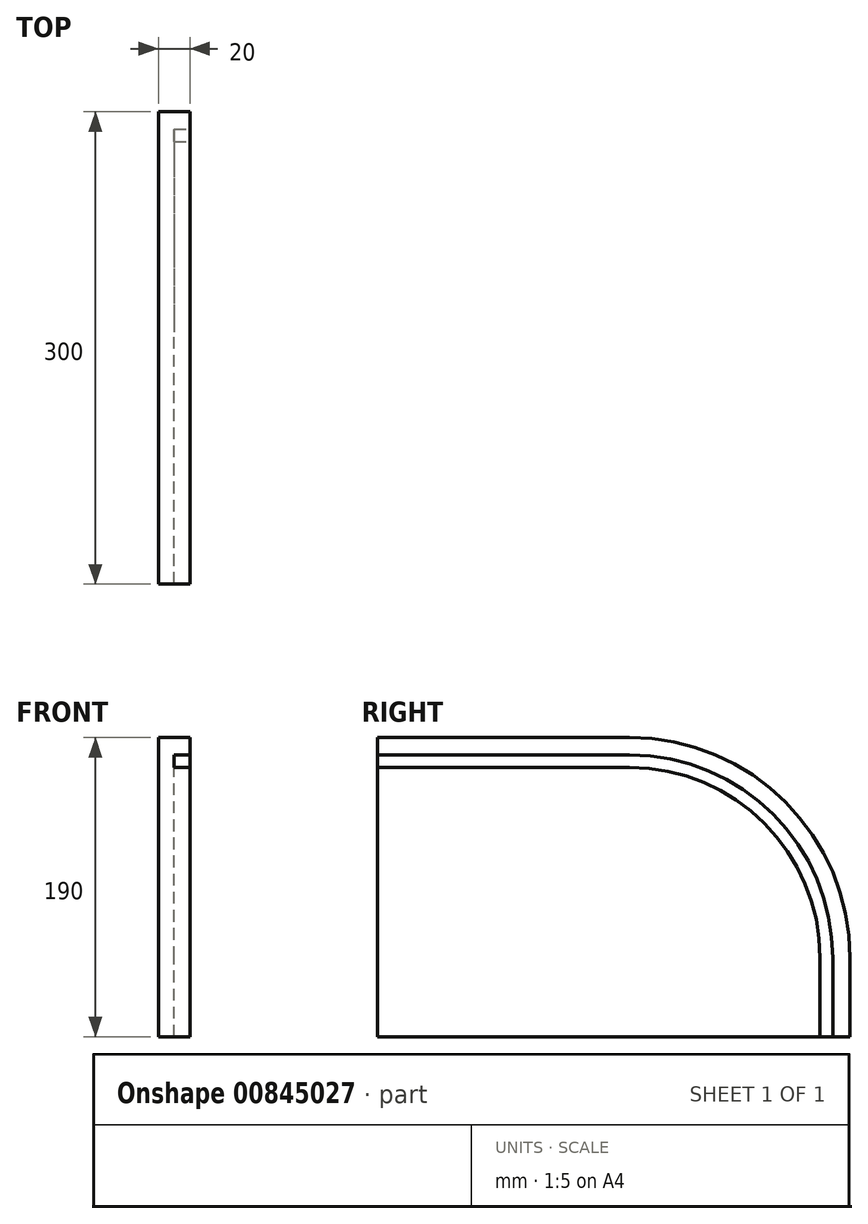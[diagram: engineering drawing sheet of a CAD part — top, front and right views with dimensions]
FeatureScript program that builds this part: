
annotation { "Feature Type Name" : "Feature", "Feature Type Description" : "" }
export const myFeature = defineFeature(function(context is Context, id is Id, definition is map)
    precondition{}
    {
        {
            var Q0;
            Q0=qCreatedBy(makeId("Right.planeOp"),FACE);
            var sketch = newSketch(context, id + "F0", { "sketchPlane" : qUnion([Q0])});
            skLineSegment(sketch, "E0.bottom", {"start": v(-150, 95) * mm, "end": v(150, 95) * mm});
            skLineSegment(sketch, "E0.top", {"start": v(-150, -95) * mm, "end": v(150, -95) * mm});
            skLineSegment(sketch, "E0.left", {"start": v(-150, 95) * mm, "end": v(-150, -95) * mm});
            skLineSegment(sketch, "E0.right", {"start": v(150, 95) * mm, "end": v(150, -95) * mm});
            skPoint(sketch, "E0.middle", {"position": v(0, 0) * mm});
            skLineSegment(sketch, "E1", {"start": v(150, -95) * mm, "end": v(-150, -95) * mm});
            skSolve(sketch);
        }
        {
            var Q0;
            Q0=makeQuery(id+"F0.imprint","IMPRINT",FACE,{"disambiguationData":[TD([[makeQuery(id+"F0.imprint","IMPRINT",EDGE,{"derivedFrom":sQuery(id+"F0.wireOp",EDGE,"E0.bottom")}),-1.0]])]});
            extrude(context, id + "F1", {"entities" : qUnion([Q0]), "depth" : 20 * mm, "offsetDistance" : 25 * mm});
        }
        {
            var Q0;
            Q0=makeQuery(id+"F1.opExtrude","SWEPT_EDGE",EDGE,{"disambiguationData":[OSD([sQuery(id+"F0.wireOp",EDGE,"E0.bottom"),sQuery(id+"F0.wireOp",EDGE,"E0.right")])]});
            fillet(context, id + "F2", {"entities" : qUnion([Q0]), "radius" : 140 * mm, "tangentPropagation" : true, "allowEdgeOverflow" : false});
        }
        {
            var Q0;
            Q0=makeQuery(id+"F1.opExtrude","CAP_FACE",FACE,{"disambiguationData":[OSD([sQuery(id+"F0.wireOp",EDGE,"E0.bottom"),sQuery(id+"F0.wireOp",EDGE,"E0.left"),sQuery(id+"F0.wireOp",EDGE,"E0.right"),sQuery(id+"F0.wireOp",EDGE,"E1")])],"isStart":false});
            var sketch = newSketch(context, id + "F3", { "sketchPlane" : qUnion([Q0])});
            skPoint(sketch, "E2", {"position": v(139, -95) * mm});
            skPoint(sketch, "E3", {"position": v(131, -95) * mm});
            skPoint(sketch, "E4", {"position": v(-150, 84) * mm});
            skPoint(sketch, "E5", {"position": v(-150, 76) * mm});
            skLineSegment(sketch, "E6", {"start": v(139, -95) * mm, "end": v(139, -45) * mm});
            skLineSegment(sketch, "E7", {"start": v(131, -95) * mm, "end": v(131, -45) * mm});
            skLineSegment(sketch, "E8", {"start": v(-150, 84) * mm, "end": v(10, 84) * mm});
            skLineSegment(sketch, "E9", {"start": v(-150, 76) * mm, "end": v(10, 76) * mm});
            skArc(sketch, "E10", {"start": v(139, -45) * mm, "mid": v(101.22, 46.22) * mm, "end": v(10, 84) * mm});
            skArc(sketch, "E11", {"start": v(131, -45) * mm, "mid": v(95.56, 40.56) * mm, "end": v(10, 76) * mm});
            skSolve(sketch);
        }
        {
            var Q0;
            {var subQ1=sQuery(id+"F3.wireOp",EDGE,"E6");Q0=makeQuery(id+"F3.imprint","IMPRINT",FACE,{"disambiguationData":[TD([[makeQuery(id+"F3.imprint","IMPRINT",EDGE,{"derivedFrom":subQ1}),1.0]])]});}
            extrude(context, id + "F4", {"entities" : qUnion([Q0]), "operationType" : NewBodyOperationType.REMOVE, "oppositeDirection" : true, "depth" : 10 * mm, "offsetDistance" : 25 * mm});
        }
    });
